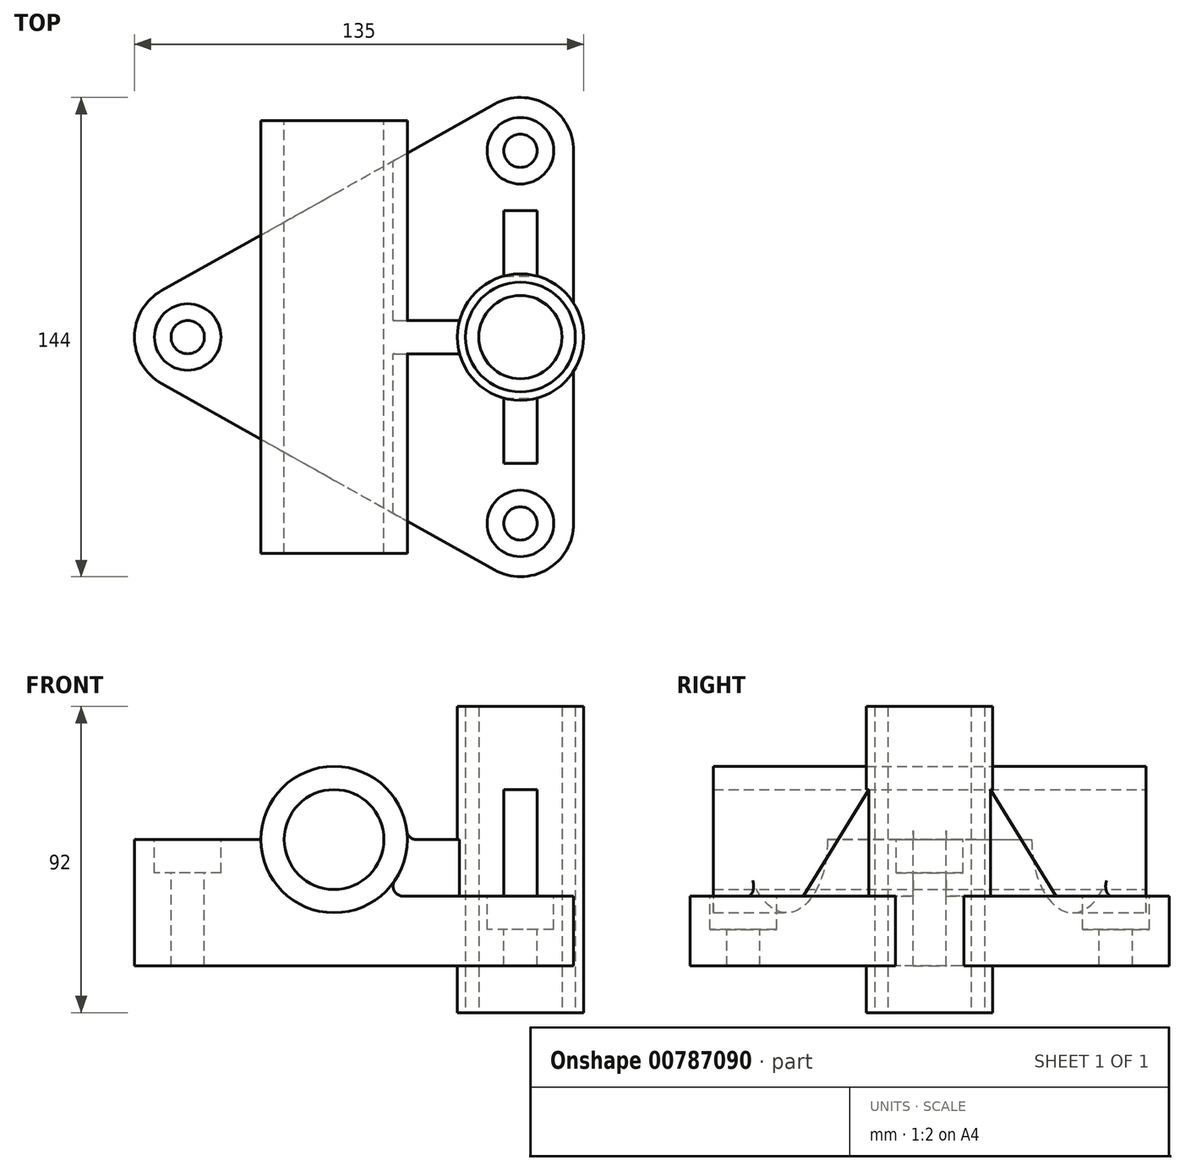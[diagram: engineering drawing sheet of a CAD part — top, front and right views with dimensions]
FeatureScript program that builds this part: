
annotation { "Feature Type Name" : "Feature", "Feature Type Description" : "" }
export const myFeature = defineFeature(function(context is Context, id is Id, definition is map)
    precondition{}
    {
        {
            var Q0;
            Q0=qCreatedBy(makeId("Front.planeOp"),FACE);
            var sketch = newSketch(context, id + "F0", { "sketchPlane" : qUnion([Q0])});
            skCircle(sketch, "E0", {"center": v(0, 0) * mm, "radius": 15 * mm});
            skCircle(sketch, "E1", {"center": v(0, 0) * mm, "radius": 22 * mm});
            skLineSegment(sketch, "E2", {"start": v(-22, 0) * mm, "end": v(-57, 0) * mm});
            skLineSegment(sketch, "E3", {"start": v(-57, 0) * mm, "end": v(-57, -38) * mm});
            skLineSegment(sketch, "E4", {"start": v(37, 0) * mm, "end": v(22, 0) * mm});
            skLineSegment(sketch, "E5", {"start": v(37, -38) * mm, "end": v(-57, -38) * mm});
            skLineSegment(sketch, "E6", {"start": v(13.96, -17) * mm, "end": v(72, -17) * mm});
            skLineSegment(sketch, "E7", {"start": v(37, -38) * mm, "end": v(72, -38) * mm});
            skLineSegment(sketch, "E8", {"start": v(72, -38) * mm, "end": v(72, -17) * mm});
            skLineSegment(sketch, "E9", {"start": v(37, -38) * mm, "end": v(37, -52) * mm});
            skLineSegment(sketch, "E10", {"start": v(37, -52) * mm, "end": v(75, -52) * mm});
            skLineSegment(sketch, "E11", {"start": v(75, -52) * mm, "end": v(75, 23) * mm});
            skLineSegment(sketch, "E12", {"start": v(75, 23) * mm, "end": v(37, 23) * mm});
            skLineSegment(sketch, "E13", {"start": v(37, 23) * mm, "end": v(37, 0) * mm});
            skLineSegment(sketch, "E14", {"start": v(56, 23) * mm, "end": v(56, -52) * mm, "construction": true});
            skLineSegment(sketch, "E15", {"start": v(39.5, 23) * mm, "end": v(39.5, -17) * mm});
            skLineSegment(sketch, "E16", {"start": v(39.5, -38) * mm, "end": v(39.5, -52) * mm});
            skLineSegment(sketch, "E17.MirrorCS", {"start": v(72.5, 23) * mm, "end": v(72.5, -17) * mm});
            skLineSegment(sketch, "E18.MirrorCS", {"start": v(72.5, -38) * mm, "end": v(72.5, -52) * mm});
            skLineSegment(sketch, "E19", {"start": v(72.5, -17) * mm, "end": v(72.5, -38) * mm});
            skLineSegment(sketch, "E20", {"start": v(43.5, 23) * mm, "end": v(43.5, -17) * mm});
            skLineSegment(sketch, "E21", {"start": v(43.5, -38) * mm, "end": v(43.5, -52) * mm});
            skLineSegment(sketch, "E22.MirrorCS", {"start": v(68.5, 23) * mm, "end": v(68.5, -17) * mm});
            skLineSegment(sketch, "E23.MirrorCS", {"start": v(68.5, -38) * mm, "end": v(68.5, -52) * mm});
            skLineSegment(sketch, "E24", {"start": v(37, 0) * mm, "end": v(37, -17) * mm});
            skLineSegment(sketch, "E25", {"start": v(22, 0) * mm, "end": v(22, -17) * mm});
            skSolve(sketch);
        }
        {
            var Q0;
            Q0=qCreatedBy(makeId("Top.planeOp"),FACE);
            var sketch = newSketch(context, id + "F1", { "sketchPlane" : qUnion([Q0])});
            skCircle(sketch, "E26", {"center": v(56, 0) * mm, "radius": 19 * mm});
            skCircle(sketch, "E27", {"center": v(56, 0) * mm, "radius": 16.5 * mm});
            skLineSegment(sketch, "E28", {"start": v(0, 65) * mm, "end": v(22, 65) * mm, "construction": true});
            skLineSegment(sketch, "E29", {"start": v(22, 65) * mm, "end": v(22, -65) * mm, "construction": true});
            skLineSegment(sketch, "E30", {"start": v(22, -65) * mm, "end": v(0, -65) * mm, "construction": true});
            skLineSegment(sketch, "E31.MirrorCS", {"start": v(-22, 65) * mm, "end": v(-22, -65) * mm, "construction": true});
            skLineSegment(sketch, "E32.MirrorCS", {"start": v(0, 65) * mm, "end": v(-22, 65) * mm, "construction": true});
            skLineSegment(sketch, "E33.MirrorCS", {"start": v(-22, -65) * mm, "end": v(0, -65) * mm, "construction": true});
            skLineSegment(sketch, "E34", {"start": v(72, 0) * mm, "end": v(72, 83.3) * mm});
            skLineSegment(sketch, "E35.MirrorCS", {"start": v(72, 0) * mm, "end": v(72, -83.3) * mm});
            skLineSegment(sketch, "E36", {"start": v(-76.75, 0) * mm, "end": v(72, 83.3) * mm});
            skLineSegment(sketch, "E37.MirrorCS", {"start": v(-76.75, 0) * mm, "end": v(72, -83.3) * mm});
            skLineSegment(sketch, "E38", {"start": v(22, 55.3) * mm, "end": v(22, -55.3) * mm});
            skLineSegment(sketch, "E39", {"start": v(-22, 30.66) * mm, "end": v(-22, -30.66) * mm});
            skLineSegment(sketch, "E40", {"start": v(22, 5) * mm, "end": v(37.67, 5) * mm});
            skLineSegment(sketch, "E41.MirrorCS", {"start": v(22, -5) * mm, "end": v(37.67, -5) * mm});
            skLineSegment(sketch, "E42", {"start": v(51, -18.33) * mm, "end": v(51, -38) * mm});
            skLineSegment(sketch, "E43", {"start": v(51, -38) * mm, "end": v(61, -38) * mm});
            skLineSegment(sketch, "E44", {"start": v(61, -38) * mm, "end": v(61, -18.33) * mm});
            skPoint(sketch, "E45", {"position": v(56, -38) * mm});
            skLineSegment(sketch, "E46.MirrorCS", {"start": v(51, 38) * mm, "end": v(61, 38) * mm});
            skPoint(sketch, "E47.MirrorP", {"position": v(56, 38) * mm});
            skLineSegment(sketch, "E48.MirrorCS", {"start": v(61, 38) * mm, "end": v(61, 18.33) * mm});
            skLineSegment(sketch, "E49.MirrorCS", {"start": v(51, 18.33) * mm, "end": v(51, 38) * mm});
            skCircle(sketch, "E50", {"center": v(-44, 0) * mm, "radius": 5 * mm});
            skLineSegment(sketch, "E51", {"start": v(72, 56) * mm, "end": v(56, 56) * mm, "construction": true});
            skLineSegment(sketch, "E52", {"start": v(48.18, 69.96) * mm, "end": v(56, 56) * mm, "construction": true});
            skCircle(sketch, "E53", {"center": v(56, 56) * mm, "radius": 5 * mm});
            skCircle(sketch, "E54.MirrorC", {"center": v(56, -56) * mm, "radius": 5 * mm});
            skLineSegment(sketch, "E55", {"start": v(-44, 0) * mm, "end": v(-51.82, 13.96) * mm, "construction": true});
            skCircle(sketch, "E56", {"center": v(56, 0) * mm, "radius": 12.5 * mm});
            skSolve(sketch);
        }
        {
            var Q0;
            Q0=makeQuery(id+"F1.imprint","IMPRINT",FACE,{"disambiguationData":[TD([[makeQuery(id+"F1.imprint","IMPRINT",EDGE,{"derivedFrom":sQuery(id+"F1.wireOp",EDGE,"L6iEjGQy-qSCQ-OCm5-ewh1-9Dsv9sjEkAjd")}),-1.0]])]});
            var Q1;
            Q1=makeQuery(id+"F1.imprint","IMPRINT",FACE,{"disambiguationData":[TD([[makeQuery(id+"F1.imprint","IMPRINT",EDGE,{"derivedFrom":sQuery(id+"F1.wireOp",EDGE,"1e10526e-26bc-44a2-a549-5cfb0348db5f0.MirrorC")}),1.0]])]});
            var Q2;
            Q2=makeQuery(id+"F1.imprint","IMPRINT",FACE,{"disambiguationData":[TD([[makeQuery(id+"F1.imprint","IMPRINT",EDGE,{"derivedFrom":sQuery(id+"F1.wireOp",EDGE,"aPyAnpgC-WgSY-FOYK-2oii-6kUxiswCP9k3")}),-1.0]])]});
            var Q3;
            Q3=makeQuery(id+"F1.imprint","IMPRINT",FACE,{"disambiguationData":[TD([[makeQuery(id+"F1.imprint","IMPRINT",EDGE,{"derivedFrom":sQuery(id+"F1.wireOp",EDGE,"L6iEjGQy-qSCQ-OCm5-ewh1-9Dsv9sjEkAjd")}),1.0]])]});
            var Q4;
            Q4=makeQuery(id+"F1.imprint","IMPRINT",FACE,{"disambiguationData":[TD([[makeQuery(id+"F1.imprint","IMPRINT",EDGE,{"derivedFrom":sQuery(id+"F1.wireOp",EDGE,"aPyAnpgC-WgSY-FOYK-2oii-6kUxiswCP9k3")}),1.0]])]});
            var Q5;
            Q5=makeQuery(id+"F1.imprint","IMPRINT",FACE,{"disambiguationData":[TD([[makeQuery(id+"F1.imprint","IMPRINT",EDGE,{"derivedFrom":sQuery(id+"F1.wireOp",EDGE,"1e10526e-26bc-44a2-a549-5cfb0348db5f0.MirrorC")}),-1.0]])]});
            var Q6;
            {var subQ7=sQuery(id+"F1.wireOp",EDGE,"E40");Q6=makeQuery(id+"F1.imprint","IMPRINT",FACE,{"disambiguationData":[TD([[makeQuery(id+"F1.imprint","IMPRINT",EDGE,{"derivedFrom":subQ7}),1.0]])]});}
            var Q7;
            {var subQ5=sQuery(id+"F1.wireOp",EDGE,"E41.MirrorCS");Q7=makeQuery(id+"F1.imprint","IMPRINT",FACE,{"disambiguationData":[TD([[makeQuery(id+"F1.imprint","IMPRINT",EDGE,{"derivedFrom":subQ5}),-1.0]])]});}
            var Q8;
            {var subQ3=sQuery(id+"F1.wireOp",EDGE,"E39");Q8=makeQuery(id+"F1.imprint","IMPRINT",FACE,{"disambiguationData":[TD([[makeQuery(id+"F1.imprint","IMPRINT",EDGE,{"derivedFrom":subQ3}),-1.0]])]});}
            var Q9;
            {var subQ5=sQuery(id+"F1.wireOp",EDGE,"E39");Q9=makeQuery(id+"F1.imprint","IMPRINT",FACE,{"disambiguationData":[TD([[makeQuery(id+"F1.imprint","IMPRINT",EDGE,{"derivedFrom":subQ5}),1.0]])]});}
            var Q10;
            {var subQ0=sQuery(id+"F1.wireOp",EDGE,"E40");Q10=makeQuery(id+"F1.imprint","IMPRINT",FACE,{"disambiguationData":[TD([[makeQuery(id+"F1.imprint","IMPRINT",EDGE,{"derivedFrom":subQ0}),-1.0]])]});}
            var Q11;
            {var subQ0=sQuery(id+"F1.wireOp",EDGE,"E42");Q11=makeQuery(id+"F1.imprint","IMPRINT",FACE,{"disambiguationData":[TD([[makeQuery(id+"F1.imprint","IMPRINT",EDGE,{"derivedFrom":subQ0}),1.0]])]});}
            var Q12;
            {var subQ0=sQuery(id+"F1.wireOp",EDGE,"E48.MirrorCS");Q12=makeQuery(id+"F1.imprint","IMPRINT",FACE,{"disambiguationData":[TD([[makeQuery(id+"F1.imprint","IMPRINT",EDGE,{"derivedFrom":subQ0}),-1.0]])]});}
            extrude(context, id + "F2", {"entities" : qUnion([Q0, Q1, Q2, Q3, Q4, Q5, Q6, Q7, Q8, Q9, Q10, Q11, Q12]), "oppositeDirection" : true, "depth" : 38 * mm, "offsetDistance" : 25 * mm});
        }
        {
            var Q0;
            Q0=makeQuery(id+"F0.imprint","IMPRINT",FACE,{"disambiguationData":[TD([[makeQuery(id+"F0.imprint","IMPRINT",EDGE,{"derivedFrom":sQuery(id+"F0.wireOp",EDGE,"E0")}),-1.0]])]});
            extrude(context, id + "F3", {"entities" : qUnion([Q0]), "operationType" : NewBodyOperationType.ADD, "endBound" : BoundingType.SYMMETRIC, "depth" : 130 * mm, "offsetDistance" : 25 * mm});
        }
        {
            var Q0;
            Q0=makeQuery(id+"F0.imprint","IMPRINT",FACE,{"disambiguationData":[TD([[makeQuery(id+"F0.imprint","IMPRINT",EDGE,{"derivedFrom":sQuery(id+"F0.wireOp",EDGE,"E0")}),1.0]])]});
            extrude(context, id + "F4", {"entities" : qUnion([Q0]), "operationType" : NewBodyOperationType.REMOVE, "endBound" : BoundingType.SYMMETRIC, "oppositeDirection" : true, "depth" : 130 * mm, "offsetDistance" : 25 * mm});
        }
        {
            var Q0;
            {var subQ7=sQuery(id+"F1.wireOp",EDGE,"E40");Q0=makeQuery(id+"F1.imprint","IMPRINT",FACE,{"disambiguationData":[TD([[makeQuery(id+"F1.imprint","IMPRINT",EDGE,{"derivedFrom":subQ7}),1.0]])]});}
            var Q1;
            {var subQ5=sQuery(id+"F1.wireOp",EDGE,"E41.MirrorCS");Q1=makeQuery(id+"F1.imprint","IMPRINT",FACE,{"disambiguationData":[TD([[makeQuery(id+"F1.imprint","IMPRINT",EDGE,{"derivedFrom":subQ5}),-1.0]])]});}
            var Q2;
            {var subQ0=sQuery(id+"F1.wireOp",EDGE,"E42");Q2=makeQuery(id+"F1.imprint","IMPRINT",FACE,{"disambiguationData":[TD([[makeQuery(id+"F1.imprint","IMPRINT",EDGE,{"derivedFrom":subQ0}),1.0]])]});}
            var Q3;
            {var subQ0=sQuery(id+"F1.wireOp",EDGE,"E48.MirrorCS");Q3=makeQuery(id+"F1.imprint","IMPRINT",FACE,{"disambiguationData":[TD([[makeQuery(id+"F1.imprint","IMPRINT",EDGE,{"derivedFrom":subQ0}),-1.0]])]});}
            var Q4;
            {var subQ0=sQuery(id+"F1.wireOp",EDGE,"E40");Q4=makeQuery(id+"F1.imprint","IMPRINT",FACE,{"disambiguationData":[TD([[makeQuery(id+"F1.imprint","IMPRINT",EDGE,{"derivedFrom":subQ0}),-1.0]])]});}
            extrude(context, id + "F5", {"entities" : qUnion([Q0, Q1, Q2, Q3, Q4]), "operationType" : NewBodyOperationType.REMOVE, "oppositeDirection" : true, "depth" : 17 * mm, "offsetDistance" : 25 * mm});
        }
        {
            var Q0;
            Q0=makeQuery(id+"F2.opExtrude","SWEPT_EDGE",EDGE,{"disambiguationData":[OSD([sQuery(id+"F1.wireOp",EDGE,"E34"),sQuery(id+"F1.wireOp",EDGE,"E36")])]});
            var Q1;
            Q1=makeQuery(id+"F2.opExtrude","SWEPT_EDGE",EDGE,{"disambiguationData":[OSD([sQuery(id+"F1.wireOp",EDGE,"E35.MirrorCS"),sQuery(id+"F1.wireOp",EDGE,"E37.MirrorCS")])]});
            var Q2;
            Q2=makeQuery(id+"F2.opExtrude","SWEPT_EDGE",EDGE,{"disambiguationData":[OSD([sQuery(id+"F1.wireOp",EDGE,"E36"),sQuery(id+"F1.wireOp",EDGE,"E37.MirrorCS")])]});
            fillet(context, id + "F6", {"entities" : qUnion([Q0, Q1, Q2]), "radius" : 16 * mm, "tangentPropagation" : true, "allowEdgeOverflow" : false});
        }
        {
            var Q0;
            {var subQ0=sQuery(id+"F1.wireOp",EDGE,"E26");var subQ8=makeQuery(id+"F1.imprint","INTERSECT",VERTEX,{"derivedFrom":[subQ0,sQuery(id+"F1.wireOp",EDGE,"E48.MirrorCS")]});Q0=makeQuery(id+"F1.imprint","IMPRINT",FACE,{"disambiguationData":[TD([[makeQuery(id+"F1.imprint","IMPRINT",EDGE,{"disambiguationData":[TD([[subQ8,1.0]])],"derivedFrom":subQ0}),1.0]])]});}
            var Q1;
            {var subQ0=sQuery(id+"F1.wireOp",EDGE,"E34");var subQ1=sQuery(id+"F1.wireOp",EDGE,"E26");var subQ2=makeQuery(id+"F1.imprint","INTERSECT",VERTEX,{"derivedFrom":[subQ1,subQ0]});Q1=makeQuery(id+"F1.imprint","IMPRINT",FACE,{"disambiguationData":[TD([[makeQuery(id+"F1.imprint","IMPRINT",EDGE,{"disambiguationData":[TD([[subQ2,1.0]])],"derivedFrom":subQ1}),1.0]])]});}
            extrude(context, id + "F7", {"entities" : qUnion([Q0, Q1]), "operationType" : NewBodyOperationType.ADD, "depth" : 40 * mm, "offsetDistance" : 25 * mm, "hasSecondDirection" : true, "secondDirectionOppositeDirection" : true, "secondDirectionDepth" : 52 * mm});
        }
        {
            var Q0;
            Q0=sQuery(id+"F1.wireOp",VERTEX,"E55.start");
            var Q1;
            Q1=makeQuery(id+"F2.opExtrude","SWEPT_BODY",BODY,{"disambiguationData":[OSD([sQuery(id+"F1.wireOp",EDGE,"E26"),sQuery(id+"F1.wireOp",EDGE,"E34"),sQuery(id+"F1.wireOp",EDGE,"E35.MirrorCS"),sQuery(id+"F1.wireOp",EDGE,"E36"),sQuery(id+"F1.wireOp",EDGE,"E37.MirrorCS"),sQuery(id+"F1.wireOp",EDGE,"E50"),sQuery(id+"F1.wireOp",EDGE,"E53"),sQuery(id+"F1.wireOp",EDGE,"E54.MirrorC")])]});
            hole(context, id + "F8", {"style" : HoleStyle.C_BORE, "endStyle" : HoleEndStyle.BLIND, "holeDiameter" : 10 * mm, "cBoreDiameter" : 20 * mm, "cBoreDepth" : 10 * mm, "majorDiameter" : 5 * mm, "holeDepth" : 38 * mm, "isTappedThrough" : true, "tappedDepth" : 12 * mm, "tapClearance" : 3, "locations" : qUnion([Q0]), "scope" : qUnion([Q1])});
        }
        {
            var Q0;
            Q0=makeQuery(id+"F1.imprint","IMPRINT",FACE,{"disambiguationData":[TD([[makeQuery(id+"F1.imprint","IMPRINT",EDGE,{"derivedFrom":sQuery(id+"F1.wireOp",EDGE,"E56")}),-1.0]])]});
            var Q1;
            {var subQ0=sQuery(id+"F1.wireOp",EDGE,"E34");var subQ1=sQuery(id+"F1.wireOp",EDGE,"E27");var subQ2=makeQuery(id+"F1.imprint","INTERSECT",VERTEX,{"derivedFrom":[subQ1,subQ0]});Q1=makeQuery(id+"F1.imprint","IMPRINT",FACE,{"disambiguationData":[TD([[makeQuery(id+"F1.imprint","IMPRINT",EDGE,{"disambiguationData":[TD([[subQ2,1.0]])],"derivedFrom":subQ1}),1.0]])]});}
            var Q2;
            Q2=makeQuery(id+"F7.opExtrude","CAP_FACE",FACE,{"disambiguationData":[OSD([sQuery(id+"F1.wireOp",EDGE,"E26"),sQuery(id+"F1.wireOp",EDGE,"E27")])],"isStart":false});
            var Q3;
            Q3=makeQuery(id+"F7.opExtrude","CAP_FACE",FACE,{"disambiguationData":[OSD([sQuery(id+"F1.wireOp",EDGE,"E26"),sQuery(id+"F1.wireOp",EDGE,"E27")])],"isStart":true});
            extrude(context, id + "F9", {"entities" : qUnion([Q0, Q1]), "endBound" : BoundingType.UP_TO_SURFACE, "depth" : 25 * mm, "endBoundEntityFace" : qUnion([Q2]), "offsetDistance" : 25 * mm, "hasSecondDirection" : true, "secondDirectionBound" : SecondDirectionBoundingType.UP_TO_SURFACE, "secondDirectionOppositeDirection" : true, "secondDirectionDepth" : 25 * mm, "secondDirectionBoundEntityFace" : qUnion([Q3])});
        }
        {
            var Q0;
            Q0=makeQuery(id+"F5.boolean.opBoolean","COPY",FACE,{"derivedFrom":makeQuery(id+"F5.opExtrude","CAP_FACE",FACE,{"disambiguationData":[OSD([sQuery(id+"F1.wireOp",EDGE,"E26"),sQuery(id+"F1.wireOp",EDGE,"E35.MirrorCS"),sQuery(id+"F1.wireOp",EDGE,"E37.MirrorCS"),sQuery(id+"F1.wireOp",EDGE,"E38"),sQuery(id+"F1.wireOp",EDGE,"E41.MirrorCS"),sQuery(id+"F1.wireOp",EDGE,"E54.MirrorC")])],"isStart":false})});
            var sketch = newSketch(context, id + "F10", { "sketchPlane" : qUnion([Q0])});
            skCircle(sketch, "E57", {"center": v(56, 0) * mm, "radius": 19 * mm});
            skLineSegment(sketch, "E58", {"start": v(56, 40.17) * mm, "end": v(56, -39.45) * mm, "construction": true});
            skLineSegment(sketch, "E59", {"start": v(61, 18.33) * mm, "end": v(61, 38) * mm});
            skLineSegment(sketch, "E60", {"start": v(61, 38) * mm, "end": v(56, 38) * mm});
            skLineSegment(sketch, "E61.MirrorCS", {"start": v(51, 18.33) * mm, "end": v(51, 38) * mm});
            skLineSegment(sketch, "E62.MirrorCS", {"start": v(51, 38) * mm, "end": v(56, 38) * mm});
            skLineSegment(sketch, "E63.MirrorCS", {"start": v(61, -18.33) * mm, "end": v(61, -38) * mm});
            skLineSegment(sketch, "E64.MirrorCS", {"start": v(51, -38) * mm, "end": v(56, -38) * mm});
            skLineSegment(sketch, "E65.MirrorCS", {"start": v(61, -38) * mm, "end": v(56, -38) * mm});
            skLineSegment(sketch, "E66.MirrorCS", {"start": v(51, -18.33) * mm, "end": v(51, -38) * mm});
            skPoint(sketch, "E67", {"position": v(56, 56) * mm});
            skPoint(sketch, "E68.MirrorP", {"position": v(56, -56) * mm});
            skSolve(sketch);
        }
        {
            var Q0;
            {var subQ0=sQuery(id+"F10.wireOp",EDGE,"E63.MirrorCS");Q0=makeQuery(id+"F10.imprint","IMPRINT",FACE,{"disambiguationData":[TD([[makeQuery(id+"F10.imprint","IMPRINT",EDGE,{"derivedFrom":subQ0}),-1.0]])]});}
            var Q1;
            {var subQ1=sQuery(id+"F10.wireOp",EDGE,"E59");Q1=makeQuery(id+"F10.imprint","IMPRINT",FACE,{"disambiguationData":[TD([[makeQuery(id+"F10.imprint","IMPRINT",EDGE,{"derivedFrom":subQ1}),1.0]])]});}
            extrude(context, id + "F11", {"entities" : qUnion([Q0, Q1]), "operationType" : NewBodyOperationType.ADD, "depth" : 32 * mm, "offsetDistance" : 25 * mm});
        }
        {
            var Q0;
            Q0=makeQuery(id+"F11.opExtrude","SWEPT_FACE",FACE,{"disambiguationData":[OSD([sQuery(id+"F10.wireOp",EDGE,"E63.MirrorCS")])]});
            var sketch = newSketch(context, id + "F12", { "sketchPlane" : qUnion([Q0])});
            skLineSegment(sketch, "E69", {"start": v(-38, -17) * mm, "end": v(-18.33, 15) * mm});
            skLineSegment(sketch, "E70", {"start": v(-18.33, 15) * mm, "end": v(-38, 15) * mm});
            skLineSegment(sketch, "E71", {"start": v(-38, 15) * mm, "end": v(-38, -17) * mm});
            skLineSegment(sketch, "E72.MirrorCS", {"start": v(18.33, 15) * mm, "end": v(38, 15) * mm});
            skLineSegment(sketch, "E73.MirrorCS", {"start": v(38, -17) * mm, "end": v(18.33, 15) * mm});
            skLineSegment(sketch, "E74.MirrorCS", {"start": v(38, 15) * mm, "end": v(38, -17) * mm});
            skSolve(sketch);
        }
        {
            var Q0;
            Q0=makeQuery(id+"F12.imprint","IMPRINT",FACE,{"disambiguationData":[TD([[makeQuery(id+"F12.imprint","IMPRINT",EDGE,{"derivedFrom":sQuery(id+"F12.wireOp",EDGE,"E69")}),1.0]])]});
            var Q1;
            Q1=makeQuery(id+"F12.imprint","IMPRINT",FACE,{"disambiguationData":[TD([[makeQuery(id+"F12.imprint","IMPRINT",EDGE,{"derivedFrom":sQuery(id+"F12.wireOp",EDGE,"E72.MirrorCS")}),-1.0]])]});
            extrude(context, id + "F13", {"entities" : qUnion([Q0, Q1]), "operationType" : NewBodyOperationType.REMOVE, "oppositeDirection" : true, "depth" : 10 * mm, "offsetDistance" : 25 * mm});
        }
        {
            var Q0;
            Q0=sQuery(id+"F10.wireOp",VERTEX,"E67");
            var Q1;
            Q1=sQuery(id+"F10.wireOp",VERTEX,"E68.MirrorP");
            var Q2;
            Q2=makeQuery(id+"F2.opExtrude","SWEPT_BODY",BODY,{"disambiguationData":[OSD([sQuery(id+"F1.wireOp",EDGE,"E26"),sQuery(id+"F1.wireOp",EDGE,"E34"),sQuery(id+"F1.wireOp",EDGE,"E35.MirrorCS"),sQuery(id+"F1.wireOp",EDGE,"E36"),sQuery(id+"F1.wireOp",EDGE,"E37.MirrorCS"),sQuery(id+"F1.wireOp",EDGE,"E50"),sQuery(id+"F1.wireOp",EDGE,"E53"),sQuery(id+"F1.wireOp",EDGE,"E54.MirrorC")])]});
            hole(context, id + "F14", {"style" : HoleStyle.C_BORE, "endStyle" : HoleEndStyle.BLIND, "holeDiameter" : 10 * mm, "cBoreDiameter" : 20 * mm, "cBoreDepth" : 10 * mm, "majorDiameter" : 5 * mm, "holeDepth" : 38 * mm, "isTappedThrough" : true, "tappedDepth" : 12 * mm, "tapClearance" : 3, "locations" : qUnion([Q0, Q1]), "scope" : qUnion([Q2])});
        }
        {
            var Q0;
            {var subQ0=sQuery(id+"F1.wireOp",EDGE,"E40");Q0=makeQuery(id+"F1.imprint","IMPRINT",FACE,{"disambiguationData":[TD([[makeQuery(id+"F1.imprint","IMPRINT",EDGE,{"derivedFrom":subQ0}),-1.0]])]});}
            extrude(context, id + "F15", {"entities" : qUnion([Q0]), "operationType" : NewBodyOperationType.ADD, "oppositeDirection" : true, "depth" : 17 * mm, "offsetDistance" : 25 * mm});
        }
        {
            var Q0;
            Q0=makeQuery(id+"F3.opExtrude","CAP_FACE",FACE,{"disambiguationData":[OSD([sQuery(id+"F0.wireOp",EDGE,"E0"),sQuery(id+"F0.wireOp",EDGE,"E1")])],"isStart":false});
            var sketch = newSketch(context, id + "F16", { "sketchPlane" : qUnion([Q0])});
            skCircle(sketch, "E75", {"center": v(0, 0) * mm, "radius": 22 * mm});
            skLineSegment(sketch, "E76", {"start": v(22, 0) * mm, "end": v(22, -17) * mm});
            skLineSegment(sketch, "E77", {"start": v(22, -17) * mm, "end": v(13.96, -17) * mm});
            skSolve(sketch);
        }
        {
            var Q0;
            {var subQ0=sQuery(id+"F16.wireOp",EDGE,"E76");Q0=makeQuery(id+"F16.imprint","IMPRINT",FACE,{"disambiguationData":[TD([[makeQuery(id+"F16.imprint","IMPRINT",EDGE,{"derivedFrom":subQ0}),-1.0]])]});}
            extrude(context, id + "F17", {"entities" : qUnion([Q0]), "operationType" : NewBodyOperationType.REMOVE, "oppositeDirection" : true, "depth" : 60 * mm, "offsetDistance" : 25 * mm});
        }
        {
            var Q0;
            Q0=makeQuery(id+"F3.opExtrude","CAP_FACE",FACE,{"disambiguationData":[OSD([sQuery(id+"F0.wireOp",EDGE,"E0"),sQuery(id+"F0.wireOp",EDGE,"E1")])],"isStart":true});
            var sketch = newSketch(context, id + "F18", { "sketchPlane" : qUnion([Q0])});
            skCircle(sketch, "E78.MirrorC", {"center": v(0, 0) * mm, "radius": 22 * mm});
            skLineSegment(sketch, "E79.MirrorCS", {"start": v(-22, 0) * mm, "end": v(-22, -17) * mm});
            skLineSegment(sketch, "E80.MirrorCS", {"start": v(-22, -17) * mm, "end": v(-13.96, -17) * mm});
            skSolve(sketch);
        }
        {
            var Q0;
            {var subQ0=sQuery(id+"F18.wireOp",EDGE,"E79.MirrorCS");Q0=makeQuery(id+"F18.imprint","IMPRINT",FACE,{"disambiguationData":[TD([[makeQuery(id+"F18.imprint","IMPRINT",EDGE,{"derivedFrom":subQ0}),1.0]])]});}
            extrude(context, id + "F19", {"entities" : qUnion([Q0]), "operationType" : NewBodyOperationType.REMOVE, "oppositeDirection" : true, "depth" : 60 * mm, "offsetDistance" : 25 * mm});
        }
        {
            var Q0;
            {var subQ0=sQuery(id+"F1.wireOp",EDGE,"E38");Q0=makeQuery(id+"F15.boolean.opBoolean","MERGE",EDGE,{"derivedFrom":[makeQuery(id+"F5.boolean.opBoolean","MERGE",EDGE,{"derivedFrom":[makeQuery(id+"F3.boolean.opBoolean","INTERSECT",EDGE,{"disambiguationData":[OD(0.0)],"derivedFrom":[makeQuery(id+"F2.opExtrude","CAP_FACE",FACE,{"disambiguationData":[OSD([sQuery(id+"F1.wireOp",EDGE,"E26"),sQuery(id+"F1.wireOp",EDGE,"E34"),sQuery(id+"F1.wireOp",EDGE,"E35.MirrorCS"),sQuery(id+"F1.wireOp",EDGE,"E36"),sQuery(id+"F1.wireOp",EDGE,"E37.MirrorCS"),sQuery(id+"F1.wireOp",EDGE,"E50"),sQuery(id+"F1.wireOp",EDGE,"E53"),sQuery(id+"F1.wireOp",EDGE,"E54.MirrorC")])],"isStart":true}),makeQuery(id+"F3.opExtrude","SWEPT_FACE",FACE,{"disambiguationData":[OSD([sQuery(id+"F0.wireOp",EDGE,"E1")])]})]}),makeQuery(id+"F5.opExtrude","CAP_EDGE",EDGE,{"disambiguationData":[OSD([subQ0])],"isStart":true})]}),makeQuery(id+"F15.opExtrude","CAP_EDGE",EDGE,{"disambiguationData":[OSD([subQ0])],"isStart":true})]});}
            var Q1;
            Q1=makeQuery(id+"F15.opExtrude","CAP_EDGE",EDGE,{"disambiguationData":[OSD([sQuery(id+"F1.wireOp",EDGE,"E26")])],"isStart":true});
            var Q2;
            Q2=makeQuery(id+"F17.boolean.opBoolean","COPY",EDGE,{"derivedFrom":makeQuery(id+"F17.opExtrude","SWEPT_EDGE",EDGE,{"disambiguationData":[OSD([sQuery(id+"F16.wireOp",EDGE,"E75"),sQuery(id+"F16.wireOp",EDGE,"E77")])]})});
            var Q3;
            Q3=makeQuery(id+"F19.boolean.opBoolean","COPY",EDGE,{"derivedFrom":makeQuery(id+"F19.opExtrude","SWEPT_EDGE",EDGE,{"disambiguationData":[OSD([sQuery(id+"F18.wireOp",EDGE,"E78.MirrorC"),sQuery(id+"F18.wireOp",EDGE,"E80.MirrorCS")])]})});
            var Q4;
            Q4=makeQuery(id+"F11.opExtrude","CAP_EDGE",EDGE,{"disambiguationData":[OSD([sQuery(id+"F10.wireOp",EDGE,"E63.MirrorCS")])],"isStart":true});
            var Q5;
            Q5=makeQuery(id+"F11.opExtrude","CAP_EDGE",EDGE,{"disambiguationData":[OSD([sQuery(id+"F10.wireOp",EDGE,"E59")])],"isStart":true});
            var Q6;
            Q6=makeQuery(id+"F11.opExtrude","CAP_EDGE",EDGE,{"disambiguationData":[OSD([sQuery(id+"F10.wireOp",EDGE,"E61.MirrorCS")])],"isStart":true});
            var Q7;
            Q7=makeQuery(id+"F11.opExtrude","CAP_EDGE",EDGE,{"disambiguationData":[OSD([sQuery(id+"F10.wireOp",EDGE,"E66.MirrorCS")])],"isStart":true});
            var Q8;
            Q8=makeQuery(id+"F11.opExtrude","SWEPT_EDGE",EDGE,{"disambiguationData":[OSD([sQuery(id+"F10.wireOp",EDGE,"E57"),sQuery(id+"F10.wireOp",EDGE,"E63.MirrorCS")])]});
            var Q9;
            Q9=makeQuery(id+"F11.opExtrude","SWEPT_EDGE",EDGE,{"disambiguationData":[OSD([sQuery(id+"F10.wireOp",EDGE,"E57"),sQuery(id+"F10.wireOp",EDGE,"E66.MirrorCS")])]});
            var Q10;
            Q10=makeQuery(id+"F11.opExtrude","SWEPT_EDGE",EDGE,{"disambiguationData":[OSD([sQuery(id+"F10.wireOp",EDGE,"E57"),sQuery(id+"F10.wireOp",EDGE,"E59")])]});
            var Q11;
            Q11=makeQuery(id+"F11.opExtrude","SWEPT_EDGE",EDGE,{"disambiguationData":[OSD([sQuery(id+"F10.wireOp",EDGE,"E57"),sQuery(id+"F10.wireOp",EDGE,"E61.MirrorCS")])]});
            fillet(context, id + "F20", {"entities" : qUnion([Q0, Q1, Q2, Q3, Q4, Q5, Q6, Q7, Q8, Q9, Q10, Q11]), "radius" : 3 * mm, "tangentPropagation" : true, "allowEdgeOverflow" : false});
        }
    });
